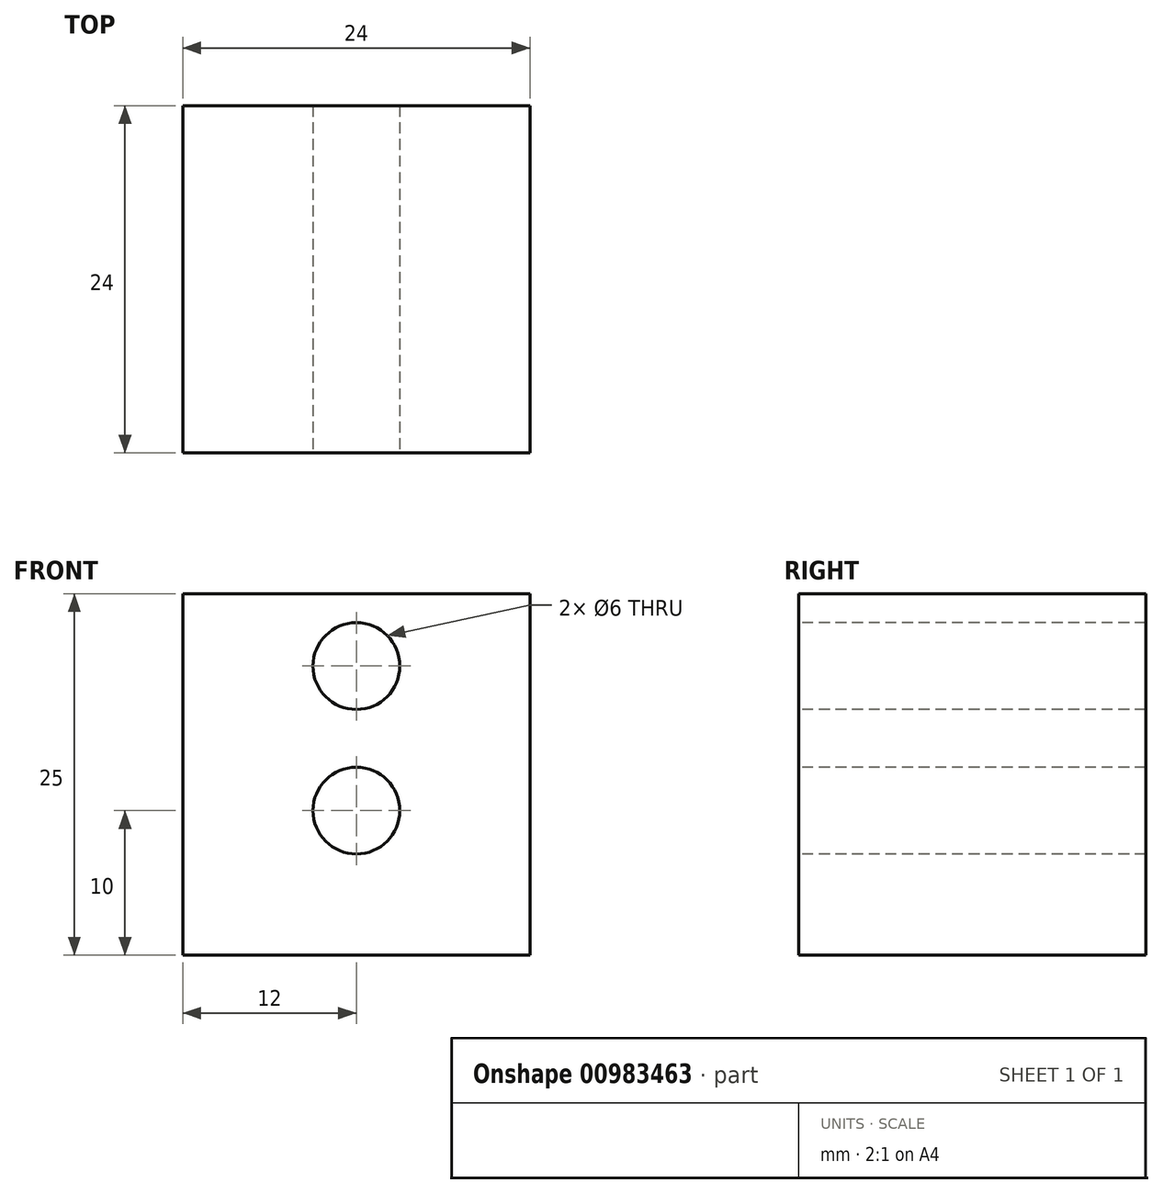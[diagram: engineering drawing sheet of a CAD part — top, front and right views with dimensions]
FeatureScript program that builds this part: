
annotation { "Feature Type Name" : "Feature", "Feature Type Description" : "" }
export const myFeature = defineFeature(function(context is Context, id is Id, definition is map)
    precondition{}
    {
        {
            var Q0;
            Q0=qCreatedBy(makeId("Top.planeOp"),FACE);
            var sketch = newSketch(context, id + "F0", { "sketchPlane" : qUnion([Q0])});
            skLineSegment(sketch, "E0.bottom", {"start": v(0, 0) * mm, "end": v(24, 0) * mm});
            skLineSegment(sketch, "E0.top", {"start": v(0, -24) * mm, "end": v(24, -24) * mm});
            skLineSegment(sketch, "E0.left", {"start": v(0, 0) * mm, "end": v(0, -24) * mm});
            skLineSegment(sketch, "E0.right", {"start": v(24, 0) * mm, "end": v(24, -24) * mm});
            skSolve(sketch);
        }
        {
            var Q0;
            Q0=qSketchRegion(id+"F0",true);
            extrude(context, id + "F1", {"entities" : qUnion([Q0]), "depth" : 25 * mm});
        }
        {
            var Q0;
            Q0=makeQuery(id+"F1.opExtrude","SWEPT_FACE",FACE,{"disambiguationData":[OSD([sQuery(id+"F0.wireOp",EDGE,"E0.top")])]});
            var sketch = newSketch(context, id + "F2", { "sketchPlane" : qUnion([Q0])});
            skLineSegment(sketch, "E1", {"start": v(12, 0) * mm, "end": v(12, 10) * mm});
            skLineSegment(sketch, "E2", {"start": v(12, 10) * mm, "end": v(12, 20) * mm});
            skSolve(sketch);
        }
        {
            var Q0;
            Q0=sQuery(id+"F2.wireOp",VERTEX,"E2.end");
            var Q1;
            Q1=sQuery(id+"F2.wireOp",VERTEX,"E2.start");
            var Q2;
            Q2=makeQuery(id+"F1.opExtrude","SWEPT_BODY",BODY,{"disambiguationData":[OSD([sQuery(id+"F0.wireOp",EDGE,"E0.bottom"),sQuery(id+"F0.wireOp",EDGE,"E0.top"),sQuery(id+"F0.wireOp",EDGE,"E0.left"),sQuery(id+"F0.wireOp",EDGE,"E0.right")])]});
            hole(context, id + "F3", {"style" : HoleStyle.SIMPLE, "endStyle" : HoleEndStyle.THROUGH, "holeDiameter" : 6 * mm, "isTappedThrough" : true, "tappedDepth" : 12 * mm, "tapClearance" : 3, "locations" : qUnion([Q0, Q1]), "scope" : qUnion([Q2])});
        }
    });
